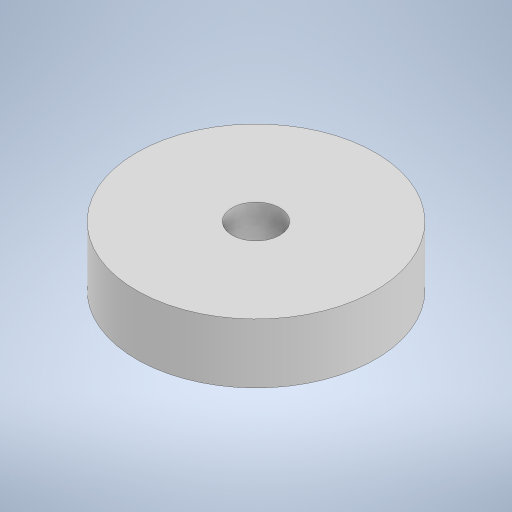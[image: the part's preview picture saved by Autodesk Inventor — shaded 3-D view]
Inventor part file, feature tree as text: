
AUTODESK INVENTOR PART (.ipt)
format: ipt  version: 2023 (Build 270158000, 158)  size: 210,944 bytes
history: native  units: mm
features: extrude x2, sketch x2, other x1
ambient origin geometry x8: Origin, YZ Plane, XZ Plane, XY Plane, X Axis, Y Axis, Z Axis, Center Point
bodies: Body1 (feature_tree)
feature tree (5):
  other  "Твердое тело1"
  extrude  "Выдавливание1"  Depth=20.0mm
  extrude  "Выдавливание2"  Depth=5.0mm TaperAngle=0.0deg
  sketch  "Эскиз1"
  sketch  "Эскиз2"
